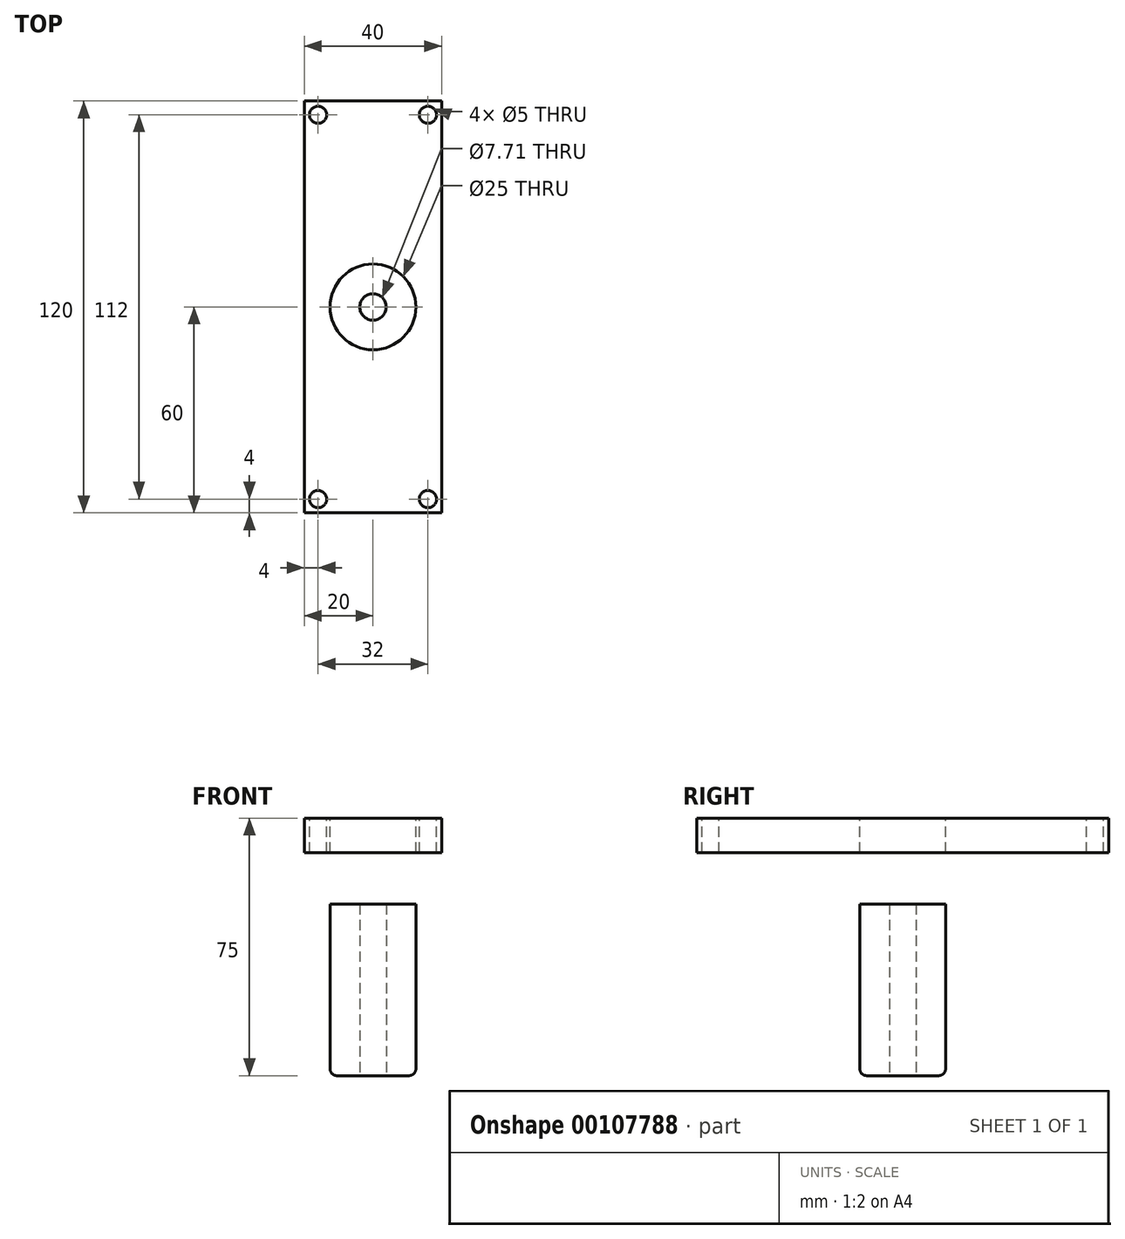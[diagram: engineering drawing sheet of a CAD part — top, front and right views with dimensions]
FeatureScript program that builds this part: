
annotation { "Feature Type Name" : "Feature", "Feature Type Description" : "" }
export const myFeature = defineFeature(function(context is Context, id is Id, definition is map)
    precondition{}
    {
        {
            var Q0;
            Q0=qCreatedBy(makeId("Top.planeOp"),FACE);
            var sketch = newSketch(context, id + "F0", { "sketchPlane" : qUnion([Q0])});
            skLineSegment(sketch, "E0.bottom", {"start": v(-20, 60) * mm, "end": v(20, 60) * mm});
            skLineSegment(sketch, "E0.top", {"start": v(-20, -60) * mm, "end": v(20, -60) * mm});
            skLineSegment(sketch, "E0.left", {"start": v(-20, 60) * mm, "end": v(-20, -60) * mm});
            skLineSegment(sketch, "E0.right", {"start": v(20, 60) * mm, "end": v(20, -60) * mm});
            skPoint(sketch, "E0.middle", {"position": v(0, 0) * mm});
            skSolve(sketch);
        }
        {
            var Q0;
            Q0 = qSketchRegion(id + "F0", true);
            extrude(context, id + "F1", {"entities" : qUnion([Q0]), "depth" : 10 * mm});
        }
        {
            var Q0;
            Q0=makeQuery(id+"F1.opExtrude","CAP_FACE",FACE,{"disambiguationData":[OSD([sQuery(id+"F0.wireOp",EDGE,"E0.bottom"),sQuery(id+"F0.wireOp",EDGE,"E0.top"),sQuery(id+"F0.wireOp",EDGE,"E0.left"),sQuery(id+"F0.wireOp",EDGE,"E0.right")])],"isStart":false});
            var sketch = newSketch(context, id + "F2", { "sketchPlane" : qUnion([Q0])});
            skCircle(sketch, "E1", {"center": v(-16, 56) * mm, "radius": 2.5 * mm});
            skCircle(sketch, "E2", {"center": v(16, 56) * mm, "radius": 2.5 * mm});
            skCircle(sketch, "E3", {"center": v(-16, -56) * mm, "radius": 2.5 * mm});
            skCircle(sketch, "E4", {"center": v(16, -56) * mm, "radius": 2.5 * mm});
            skCircle(sketch, "E5", {"center": v(0, 0) * mm, "radius": 12.5 * mm});
            skSolve(sketch);
        }
        {
            var Q0;
            Q0=makeQuery(id+"F2.imprint","IMPRINT",FACE,{"disambiguationData":[TD([[makeQuery(id+"F2.imprint","IMPRINT",EDGE,{"derivedFrom":sQuery(id+"F2.wireOp",EDGE,"E5")}),1.0]])]});
            var Q1;
            Q1=makeQuery(id+"F1.opExtrude","CAP_FACE",FACE,{"disambiguationData":[OSD([sQuery(id+"F0.wireOp",EDGE,"E0.bottom"),sQuery(id+"F0.wireOp",EDGE,"E0.top"),sQuery(id+"F0.wireOp",EDGE,"E0.left"),sQuery(id+"F0.wireOp",EDGE,"E0.right")])],"isStart":false});
            extrude(context, id + "F3", {"entities" : qUnion([Q0]), "oppositeDirection" : true, "endBoundEntityFace" : qUnion([Q1]), "depth" : 75 * mm});
        }
        {
            var Q0;
            Q0 = qSketchRegion(id + "F2", true);
            extrude(context, id + "F4", {"entities" : qUnion([Q0]), "operationType" : NewBodyOperationType.REMOVE, "oppositeDirection" : true, "depth" : 25 * mm});
        }
        {
            var Q0;
            Q0=makeQuery(id+"F3.opExtrude","CAP_EDGE",EDGE,{"disambiguationData":[OSD([sQuery(id+"F2.wireOp",EDGE,"E5")])],"isStart":false});
            fillet(context, id + "F5", {"entities" : qUnion([Q0]), "radius" : 2 * mm, "allowEdgeOverflow" : false});
        }
        {
            var Q0;
            Q0=makeQuery(id+"F3.opExtrude","CAP_FACE",FACE,{"disambiguationData":[OSD([sQuery(id+"F2.wireOp",EDGE,"E5")])],"isStart":false});
            var sketch = newSketch(context, id + "F6", { "sketchPlane" : qUnion([Q0])});
            skCircle(sketch, "E6", {"center": v(0, 0) * mm, "radius": 3.86 * mm});
            skSolve(sketch);
        }
        {
            var Q0;
            Q0 = qSketchRegion(id + "F6", true);
            extrude(context, id + "F7", {"entities" : qUnion([Q0]), "operationType" : NewBodyOperationType.REMOVE, "oppositeDirection" : true, "depth" : 70 * mm});
        }
    });
